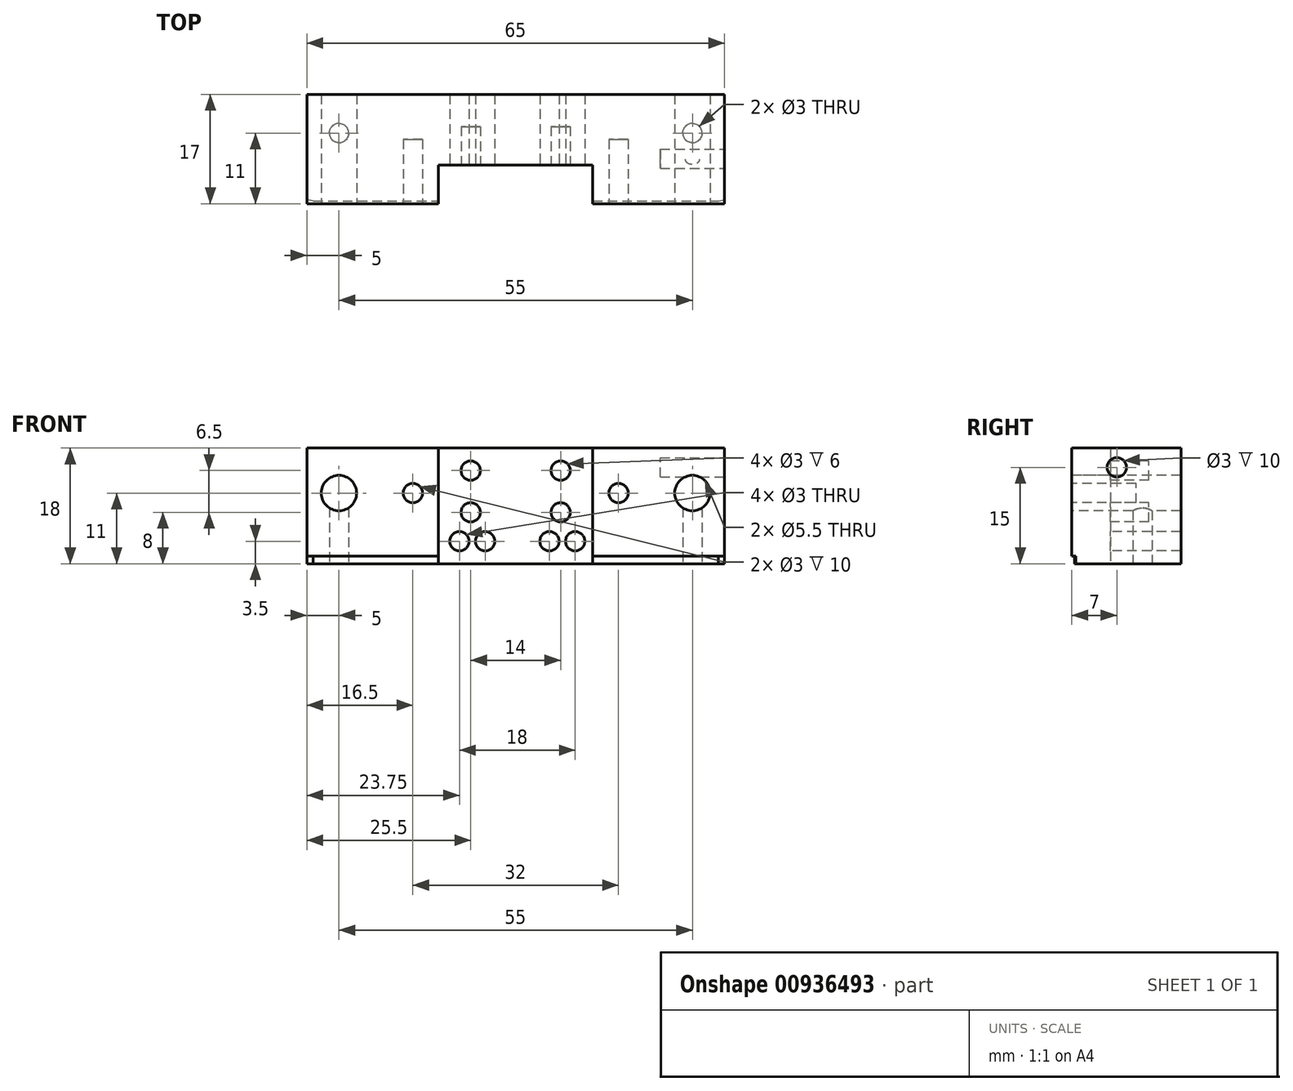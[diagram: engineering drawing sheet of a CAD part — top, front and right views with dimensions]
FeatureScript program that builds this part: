
annotation { "Feature Type Name" : "Feature", "Feature Type Description" : "" }
export const myFeature = defineFeature(function(context is Context, id is Id, definition is map)
    precondition{}
    {
        {
            var Q0;
            Q0=qCreatedBy(makeId("Front.planeOp"),FACE);
            var sketch = newSketch(context, id + "F0", { "sketchPlane" : qUnion([Q0])});
            skLineSegment(sketch, "E0.bottom", {"start": v(-32.5, -9) * mm, "end": v(32.5, -9) * mm});
            skLineSegment(sketch, "E0.top", {"start": v(-32.5, 9) * mm, "end": v(32.5, 9) * mm});
            skLineSegment(sketch, "E0.left", {"start": v(-32.5, -9) * mm, "end": v(-32.5, 9) * mm});
            skLineSegment(sketch, "E0.right", {"start": v(32.5, -9) * mm, "end": v(32.5, 9) * mm});
            skPoint(sketch, "E0.middle", {"position": v(0, 0) * mm});
            skSolve(sketch);
        }
        {
            var Q0;
            Q0 = qSketchRegion(id + "F0", true);
            extrude(context, id + "F1", {"entities" : qUnion([Q0]), "oppositeDirection" : true, "depth" : 17 * mm, "offsetDistance" : 25 * mm});
        }
        {
            var Q0;
            Q0=makeQuery(id+"F1.opExtrude","CAP_FACE",FACE,{"disambiguationData":[OSD([sQuery(id+"F0.wireOp",EDGE,"E0.bottom"),sQuery(id+"F0.wireOp",EDGE,"E0.top"),sQuery(id+"F0.wireOp",EDGE,"E0.left"),sQuery(id+"F0.wireOp",EDGE,"E0.right")])],"isStart":true});
            var sketch = newSketch(context, id + "F2", { "sketchPlane" : qUnion([Q0])});
            skLineSegment(sketch, "E1.bottom", {"start": v(-12, 9) * mm, "end": v(12, 9) * mm});
            skLineSegment(sketch, "E1.top", {"start": v(-12, -9) * mm, "end": v(12, -9) * mm});
            skLineSegment(sketch, "E1.left", {"start": v(-12, 9) * mm, "end": v(-12, -9) * mm});
            skLineSegment(sketch, "E1.right", {"start": v(12, 9) * mm, "end": v(12, -9) * mm});
            skSolve(sketch);
        }
        {
            var Q0;
            Q0 = qSketchRegion(id + "F2", true);
            extrude(context, id + "F3", {"entities" : qUnion([Q0]), "operationType" : NewBodyOperationType.REMOVE, "oppositeDirection" : true, "depth" : 6 * mm, "offsetDistance" : 25 * mm});
        }
        {
            var Q0;
            {var subQ0=sQuery(id+"F0.wireOp",EDGE,"E0.bottom");var subQ1=sQuery(id+"F0.wireOp",EDGE,"E0.top");var subQ2=sQuery(id+"F0.wireOp",EDGE,"E0.left");Q0=makeQuery(id+"F3.boolean.opBoolean","SPLIT",FACE,{"disambiguationData":[TD([makeQuery(id+"F1.opExtrude","SWEPT_FACE",FACE,{"disambiguationData":[OSD([subQ2])]})])],"derivedFrom":makeQuery(id+"F1.opExtrude","CAP_FACE",FACE,{"disambiguationData":[OSD([subQ0,subQ1,subQ2,sQuery(id+"F0.wireOp",EDGE,"E0.right")])],"isStart":true})});}
            var sketch = newSketch(context, id + "F4", { "sketchPlane" : qUnion([Q0])});
            skCircle(sketch, "E2", {"center": v(-27.5, 2) * mm, "radius": 2.75 * mm});
            skCircle(sketch, "E3", {"center": v(27.5, 2) * mm, "radius": 2.75 * mm});
            skSolve(sketch);
        }
        {
            var Q0;
            Q0 = qSketchRegion(id + "F4", true);
            extrude(context, id + "F5", {"entities" : qUnion([Q0]), "operationType" : NewBodyOperationType.REMOVE, "endBound" : BoundingType.UP_TO_NEXT, "oppositeDirection" : true, "depth" : 25 * mm, "offsetDistance" : 25 * mm});
        }
        {
            var Q0;
            {var subQ0=sQuery(id+"F0.wireOp",EDGE,"E0.bottom");var subQ1=sQuery(id+"F0.wireOp",EDGE,"E0.top");var subQ2=sQuery(id+"F0.wireOp",EDGE,"E0.left");Q0=makeQuery(id+"F3.boolean.opBoolean","SPLIT",FACE,{"disambiguationData":[TD([makeQuery(id+"F1.opExtrude","SWEPT_FACE",FACE,{"disambiguationData":[OSD([subQ2])]})])],"derivedFrom":makeQuery(id+"F1.opExtrude","CAP_FACE",FACE,{"disambiguationData":[OSD([subQ0,subQ1,subQ2,sQuery(id+"F0.wireOp",EDGE,"E0.right")])],"isStart":true})});}
            var sketch = newSketch(context, id + "F6", { "sketchPlane" : qUnion([Q0])});
            skLineSegment(sketch, "E4", {"start": v(-27.5, 2) * mm, "end": v(-16, 2) * mm});
            skLineSegment(sketch, "E5", {"start": v(-27.5, 2) * mm, "end": v(16, 2) * mm});
            skCircle(sketch, "E6", {"center": v(-16, 2) * mm, "radius": 1.5 * mm});
            skCircle(sketch, "E7", {"center": v(16, 2) * mm, "radius": 1.5 * mm});
            skSolve(sketch);
        }
        {
            var Q0;
            Q0 = qSketchRegion(id + "F6", true);
            extrude(context, id + "F7", {"entities" : qUnion([Q0]), "operationType" : NewBodyOperationType.REMOVE, "oppositeDirection" : true, "depth" : 10 * mm, "offsetDistance" : 25 * mm});
        }
        {
            var Q0;
            {var subQ0=sQuery(id+"F0.wireOp",EDGE,"E0.bottom");var subQ1=sQuery(id+"F0.wireOp",EDGE,"E0.top");var subQ2=sQuery(id+"F0.wireOp",EDGE,"E0.left");Q0=makeQuery(id+"F3.boolean.opBoolean","SPLIT",FACE,{"disambiguationData":[TD([makeQuery(id+"F1.opExtrude","SWEPT_FACE",FACE,{"disambiguationData":[OSD([subQ2])]})])],"derivedFrom":makeQuery(id+"F1.opExtrude","CAP_FACE",FACE,{"disambiguationData":[OSD([subQ0,subQ1,subQ2,sQuery(id+"F0.wireOp",EDGE,"E0.right")])],"isStart":true})});}
            var sketch = newSketch(context, id + "F8", { "sketchPlane" : qUnion([Q0])});
            skLineSegment(sketch, "E8.bottom", {"start": v(-32.5, -9) * mm, "end": v(32.5, -9) * mm});
            skLineSegment(sketch, "E8.top", {"start": v(-32.5, -7.8) * mm, "end": v(32.5, -7.8) * mm});
            skLineSegment(sketch, "E8.left", {"start": v(-32.5, -9) * mm, "end": v(-32.5, -7.8) * mm});
            skLineSegment(sketch, "E8.right", {"start": v(32.5, -9) * mm, "end": v(32.5, -7.8) * mm});
            skSolve(sketch);
        }
        {
            var Q0;
            Q0 = qSketchRegion(id + "F8", true);
            extrude(context, id + "F9", {"entities" : qUnion([Q0]), "operationType" : NewBodyOperationType.REMOVE, "oppositeDirection" : true, "depth" : .45 * mm, "offsetDistance" : 25 * mm});
        }
        {
            var Q0;
            Q0=makeQuery(id+"F1.opExtrude","SWEPT_FACE",FACE,{"disambiguationData":[OSD([sQuery(id+"F0.wireOp",EDGE,"E0.bottom")])]});
            var sketch = newSketch(context, id + "F10", { "sketchPlane" : qUnion([Q0])});
            skLineSegment(sketch, "E9", {"start": v(-32.5, -0.45) * mm, "end": v(-31.5, -0.45) * mm});
            skLineSegment(sketch, "E10", {"start": v(-31.5, -0.45) * mm, "end": v(-32.5, -0.63) * mm});
            skLineSegment(sketch, "E11", {"start": v(-32.5, -0.63) * mm, "end": v(-32.5, -0.45) * mm});
            skLineSegment(sketch, "E12", {"start": v(32.5, -0.45) * mm, "end": v(31.5, -0.45) * mm});
            skLineSegment(sketch, "E13", {"start": v(31.5, -0.45) * mm, "end": v(32.5, -0.63) * mm});
            skLineSegment(sketch, "E14", {"start": v(32.5, -0.45) * mm, "end": v(32.5, -0.63) * mm});
            skSolve(sketch);
        }
        {
            var Q0;
            Q0 = qSketchRegion(id + "F10", true);
            extrude(context, id + "F11", {"entities" : qUnion([Q0]), "operationType" : NewBodyOperationType.REMOVE, "oppositeDirection" : true, "depth" : 1.2 * mm, "offsetDistance" : 25 * mm});
        }
        {
            var Q0;
            Q0=makeQuery(id+"F3.boolean.opBoolean","COPY",FACE,{"derivedFrom":makeQuery(id+"F3.opExtrude","CAP_FACE",FACE,{"disambiguationData":[OSD([sQuery(id+"F2.wireOp",EDGE,"E1.bottom"),sQuery(id+"F2.wireOp",EDGE,"E1.top"),sQuery(id+"F2.wireOp",EDGE,"E1.left"),sQuery(id+"F2.wireOp",EDGE,"E1.right")])],"isStart":false})});
            var sketch = newSketch(context, id + "F12", { "sketchPlane" : qUnion([Q0])});
            skLineSegment(sketch, "E15", {"start": v(-12, 9) * mm, "end": v(-7, 9) * mm});
            skLineSegment(sketch, "E16", {"start": v(-7, 9) * mm, "end": v(-7, 5.5) * mm});
            skLineSegment(sketch, "E17", {"start": v(-7, 9) * mm, "end": v(-7, -1) * mm});
            skLineSegment(sketch, "E18", {"start": v(-7, 9) * mm, "end": v(7, 9) * mm});
            skLineSegment(sketch, "E19", {"start": v(7, 9) * mm, "end": v(7, 5.5) * mm});
            skLineSegment(sketch, "E20", {"start": v(7, 9) * mm, "end": v(7, -1) * mm});
            skCircle(sketch, "E21", {"center": v(-7, 5.5) * mm, "radius": 1.5 * mm});
            skCircle(sketch, "E22", {"center": v(-7, -1) * mm, "radius": 1.5 * mm});
            skCircle(sketch, "E23", {"center": v(7, 5.5) * mm, "radius": 1.5 * mm});
            skCircle(sketch, "E24", {"center": v(7, -1) * mm, "radius": 1.5 * mm});
            skSolve(sketch);
        }
        {
            var Q0;
            Q0 = qSketchRegion(id + "F12", true);
            extrude(context, id + "F13", {"entities" : qUnion([Q0]), "operationType" : NewBodyOperationType.REMOVE, "oppositeDirection" : true, "depth" : 6 * mm, "offsetDistance" : 25 * mm});
        }
        {
            var Q0;
            Q0=makeQuery(id+"F3.boolean.opBoolean","COPY",FACE,{"derivedFrom":makeQuery(id+"F3.opExtrude","CAP_FACE",FACE,{"disambiguationData":[OSD([sQuery(id+"F2.wireOp",EDGE,"E1.bottom"),sQuery(id+"F2.wireOp",EDGE,"E1.top"),sQuery(id+"F2.wireOp",EDGE,"E1.left"),sQuery(id+"F2.wireOp",EDGE,"E1.right")])],"isStart":false})});
            var sketch = newSketch(context, id + "F14", { "sketchPlane" : qUnion([Q0])});
            skCircle(sketch, "E25", {"center": v(-8.75, -5.5) * mm, "radius": 1.5 * mm});
            skCircle(sketch, "E26", {"center": v(-4.75, -5.5) * mm, "radius": 1.5 * mm});
            skCircle(sketch, "E27", {"center": v(5.25, -5.5) * mm, "radius": 1.5 * mm});
            skCircle(sketch, "E28", {"center": v(9.25, -5.5) * mm, "radius": 1.5 * mm});
            skSolve(sketch);
        }
        {
            var Q0;
            Q0 = qSketchRegion(id + "F14", true);
            extrude(context, id + "F15", {"entities" : qUnion([Q0]), "operationType" : NewBodyOperationType.REMOVE, "endBound" : BoundingType.UP_TO_NEXT, "oppositeDirection" : true, "depth" : 25 * mm, "offsetDistance" : 25 * mm});
        }
        {
            var Q0;
            Q0=makeQuery(id+"F1.opExtrude","SWEPT_FACE",FACE,{"disambiguationData":[OSD([sQuery(id+"F0.wireOp",EDGE,"E0.bottom")])]});
            var sketch = newSketch(context, id + "F16", { "sketchPlane" : qUnion([Q0])});
            skLineSegment(sketch, "E29", {"start": v(-27.5, -11) * mm, "end": v(27.5, -11) * mm});
            skCircle(sketch, "E30", {"center": v(-27.5, -11) * mm, "radius": 1.5 * mm});
            skCircle(sketch, "E31", {"center": v(27.5, -11) * mm, "radius": 1.5 * mm});
            skSolve(sketch);
        }
        {
            var Q0;
            Q0 = qSketchRegion(id + "F16", true);
            extrude(context, id + "F17", {"entities" : qUnion([Q0]), "operationType" : NewBodyOperationType.REMOVE, "oppositeDirection" : true, "depth" : 10 * mm, "offsetDistance" : 25 * mm});
        }
        {
            var Q0;
            Q0=makeQuery(id+"F1.opExtrude","SWEPT_FACE",FACE,{"disambiguationData":[OSD([sQuery(id+"F0.wireOp",EDGE,"E0.right")])]});
            var sketch = newSketch(context, id + "F18", { "sketchPlane" : qUnion([Q0])});
            skLineSegment(sketch, "E32", {"start": v(17, 9) * mm, "end": v(17, 6) * mm});
            skLineSegment(sketch, "E33", {"start": v(17, 6) * mm, "end": v(7, 6) * mm});
            skCircle(sketch, "E34", {"center": v(7, 6) * mm, "radius": 1.5 * mm});
            skSolve(sketch);
        }
        {
            var Q0;
            Q0 = qSketchRegion(id + "F18", true);
            extrude(context, id + "F19", {"entities" : qUnion([Q0]), "operationType" : NewBodyOperationType.REMOVE, "oppositeDirection" : true, "depth" : 10 * mm, "offsetDistance" : 25 * mm});
        }
    });
